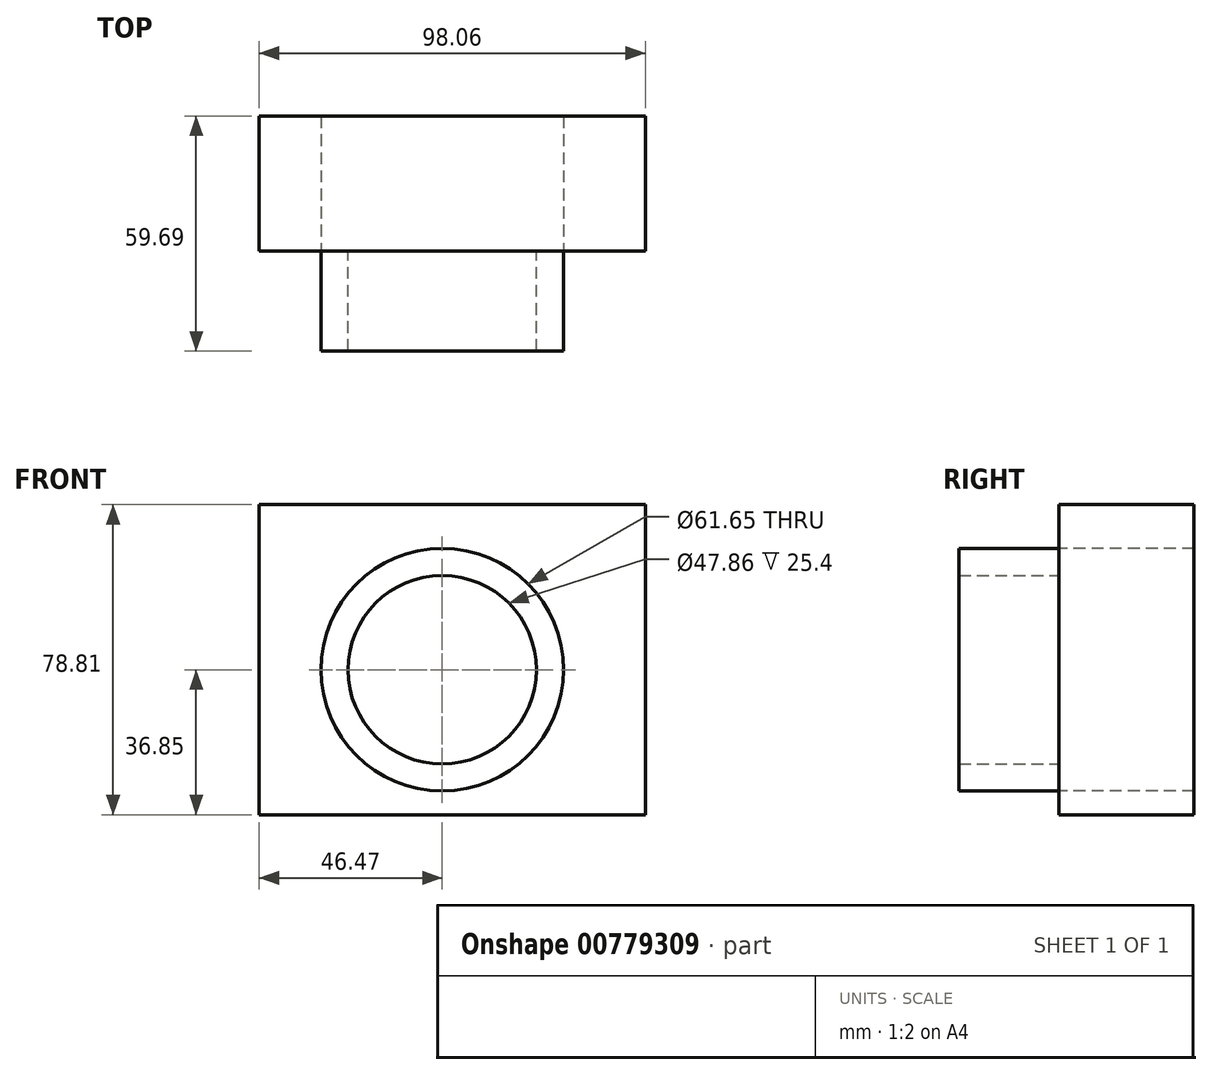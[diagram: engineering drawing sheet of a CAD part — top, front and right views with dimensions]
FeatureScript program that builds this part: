
annotation { "Feature Type Name" : "Feature", "Feature Type Description" : "" }
export const myFeature = defineFeature(function(context is Context, id is Id, definition is map)
    precondition{}
    {
        {
            var Q0;
            Q0=qCreatedBy(makeId("Front.planeOp"),FACE);
            var sketch = newSketch(context, id + "F0", { "sketchPlane" : qUnion([Q0])});
            skLineSegment(sketch, "E0.bottom", {"start": v(-46.47, 41.96) * mm, "end": v(51.59, 41.96) * mm});
            skLineSegment(sketch, "E0.top", {"start": v(-46.47, -36.85) * mm, "end": v(51.59, -36.85) * mm});
            skLineSegment(sketch, "E0.left", {"start": v(-46.47, 41.96) * mm, "end": v(-46.47, -36.85) * mm});
            skLineSegment(sketch, "E0.right", {"start": v(51.59, 41.96) * mm, "end": v(51.59, -36.85) * mm});
            skCircle(sketch, "E1", {"center": v(0, 0) * mm, "radius": 23.93 * mm});
            skCircle(sketch, "E2", {"center": v(0, 0) * mm, "radius": 30.83 * mm});
            skSolve(sketch);
        }
        {
            var Q0;
            Q0=makeQuery(id+"F0.imprint","IMPRINT",FACE,{"disambiguationData":[TD([[makeQuery(id+"F0.imprint","IMPRINT",EDGE,{"derivedFrom":sQuery(id+"F0.wireOp",EDGE,"E1")}),-1.0]])]});
            extrude(context, id + "F1", {"entities" : qUnion([Q0]), "depth" : 25.4 * mm, "offsetDistance" : 25.4 * mm});
        }
        {
            var Q0;
            Q0=makeQuery(id+"F0.imprint","IMPRINT",FACE,{"disambiguationData":[TD([[makeQuery(id+"F0.imprint","IMPRINT",EDGE,{"derivedFrom":sQuery(id+"F0.wireOp",EDGE,"E0.bottom")}),-1.0]])]});
            extrude(context, id + "F2", {"entities" : qUnion([Q0]), "oppositeDirection" : true, "depth" : 34.3 * mm, "offsetDistance" : 25.4 * mm});
        }
    });
